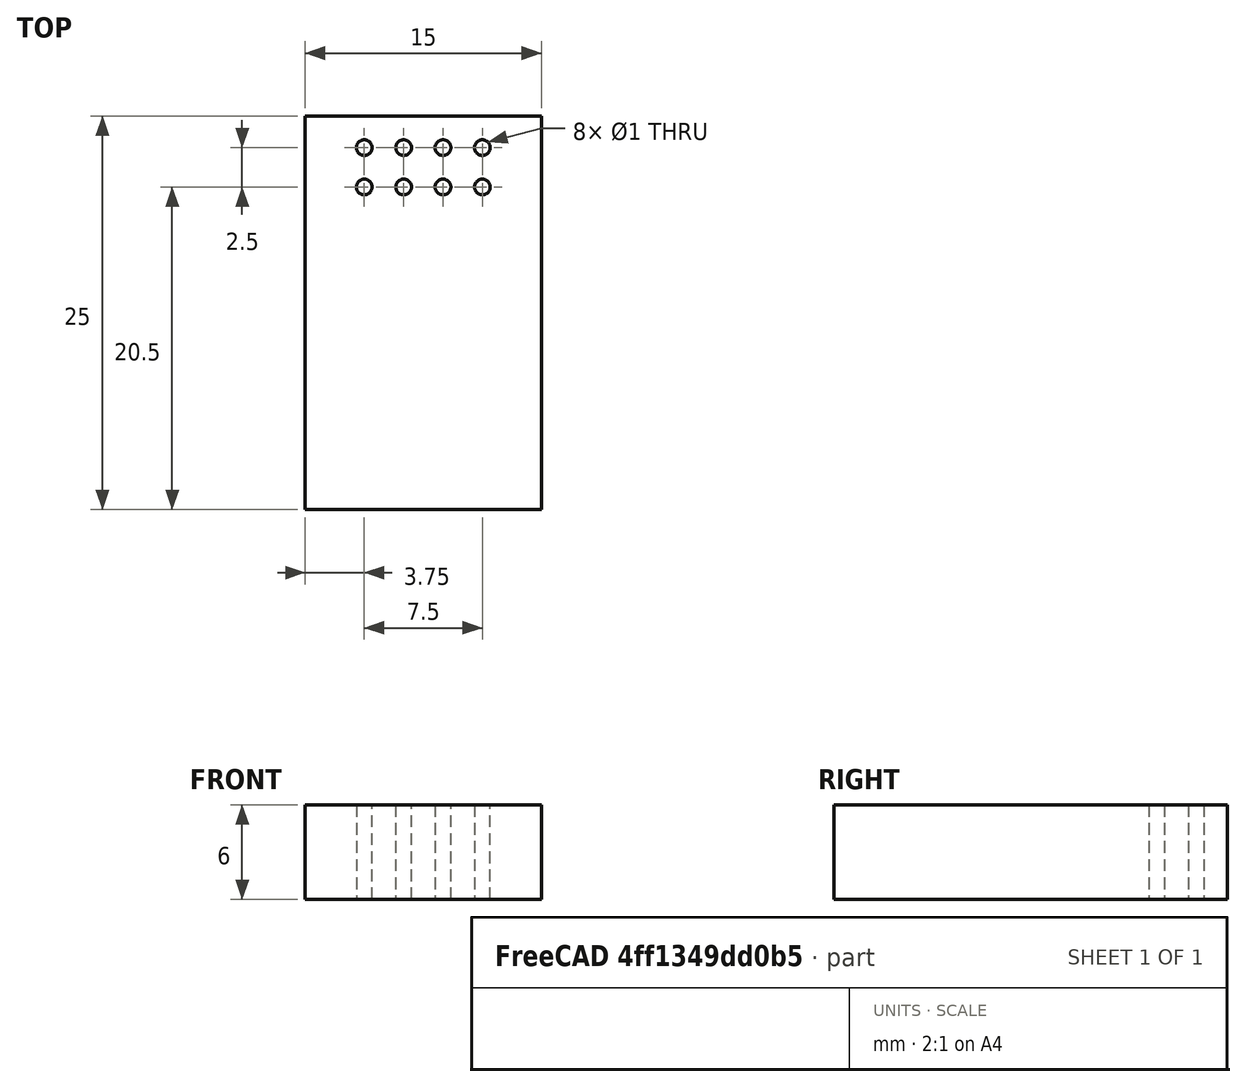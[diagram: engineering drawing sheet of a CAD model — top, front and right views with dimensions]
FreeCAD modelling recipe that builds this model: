
FCSTD DOCUMENT  (FreeCAD 0.19R24276 (Git))
Label: ESP01
License: All rights reserved
LicenseURL: http://en.wikipedia.org/wiki/All_rights_reserved
objects: Sketcher::SketchObject×1, PartDesign::Pad×1, PartDesign::Body×1
note: 4 computed .brp shape members not serialized (recipe doc carries the construction recipe); baked Part::Feature solids carry a one-line shape summary decoded from their .brp

FEATURE [Sketcher::SketchObject] Sketch
  FullyConstrained = true
  MapMode = 5
  Support = -> [XY_Plane]
  sketch-geometry (13):
    g0: LineSegment StartX=0 StartY=0 StartZ=0 EndX=15 EndY=0 EndZ=0
    g1: LineSegment StartX=15 StartY=0 StartZ=0 EndX=15 EndY=-25 EndZ=0
    g2: LineSegment StartX=15 StartY=-25 StartZ=0 EndX=0 EndY=-25 EndZ=0
    g3: LineSegment StartX=0 StartY=-25 StartZ=0 EndX=0 EndY=0 EndZ=0
    g4: Circle CenterX=3.75 CenterY=-2 CenterZ=0 NormalX=0 NormalY=0 NormalZ=1 AngleXU=0 Radius=0.5
    g5: Circle CenterX=3.75 CenterY=-4.5 CenterZ=0 NormalX=0 NormalY=0 NormalZ=1 AngleXU=0 Radius=0.5
    g6: Circle CenterX=6.25 CenterY=-2 CenterZ=0 NormalX=0 NormalY=0 NormalZ=1 AngleXU=0 Radius=0.5
    g7: Circle CenterX=6.25 CenterY=-4.5 CenterZ=0 NormalX=0 NormalY=0 NormalZ=1 AngleXU=0 Radius=0.5
    g8: Circle CenterX=8.75 CenterY=-2 CenterZ=0 NormalX=0 NormalY=0 NormalZ=1 AngleXU=0 Radius=0.5
    g9: Circle CenterX=8.75 CenterY=-4.5 CenterZ=0 NormalX=0 NormalY=0 NormalZ=1 AngleXU=0 Radius=0.5
    g10: Circle CenterX=11.25 CenterY=-2 CenterZ=0 NormalX=0 NormalY=0 NormalZ=1 AngleXU=0 Radius=0.5
    g11: Circle CenterX=11.25 CenterY=-4.5 CenterZ=0 NormalX=0 NormalY=0 NormalZ=1 AngleXU=0 Radius=0.5
    g12: LineSegment StartX=7.5 StartY=0 StartZ=0 EndX=7.5 EndY=-4.5 EndZ=0
  constraints (37):
    c: Coincident(g0,g1)
    c: Coincident(g1,g2)
    c: Coincident(g2,g3)
    c: Coincident(g3,g0)
    c: Horizontal(g0)
    c: Horizontal(g2)
    c: Vertical(g1)
    c: Vertical(g3)
    c: Coincident(g0,g-1)
    c: DistanceX(g0,g0) = 15
    c: DistanceY(g1,g1) = 25
    c: Diameter(g5) = 1
    c: Equal(g5,g4)
    c: Vertical(g4,g5)
    c: DistanceY(g5,g4) = 2.5
    c: DistanceY(g4,g0) = 2
    c: Equal(g5,g7) = 1
    c: Equal(g7,g6)
    c: Vertical(g6,g7)
    c: DistanceY(g7,g6) = 2.5
    c: Horizontal(g4,g6)
    c: DistanceX(g5,g7) = 2.5
    c: Equal(g5,g9) = 1
    c: Equal(g9,g8)
    c: Vertical(g8,g9)
    c: DistanceY(g9,g8) = 2.5
    c: Equal(g9,g11) = 1
    c: Equal(g11,g10)
    c: Vertical(g10,g11)
    c: DistanceY(g11,g10) = 2.5
    c: Horizontal(g8,g10)
    c: DistanceX(g9,g11) = 2.5
    c: Horizontal(g7,g9)
    c: DistanceX(g7,g9) = 2.5
    c: Vertical(g12)
    c: Symmetric(g0,g0,g12)
    c: Symmetric(g7,g9,g12)
FEATURE [PartDesign::Pad] Pad
  Direction = (1,1,1)
  Length = 6
  Length2 = 100
  Profile = -> Sketch
  Type = 0
FEATURE [PartDesign::Body] Body
  Group = -> [Sketch,Pad]
  Origin = -> Origin
  Tip = -> Pad
